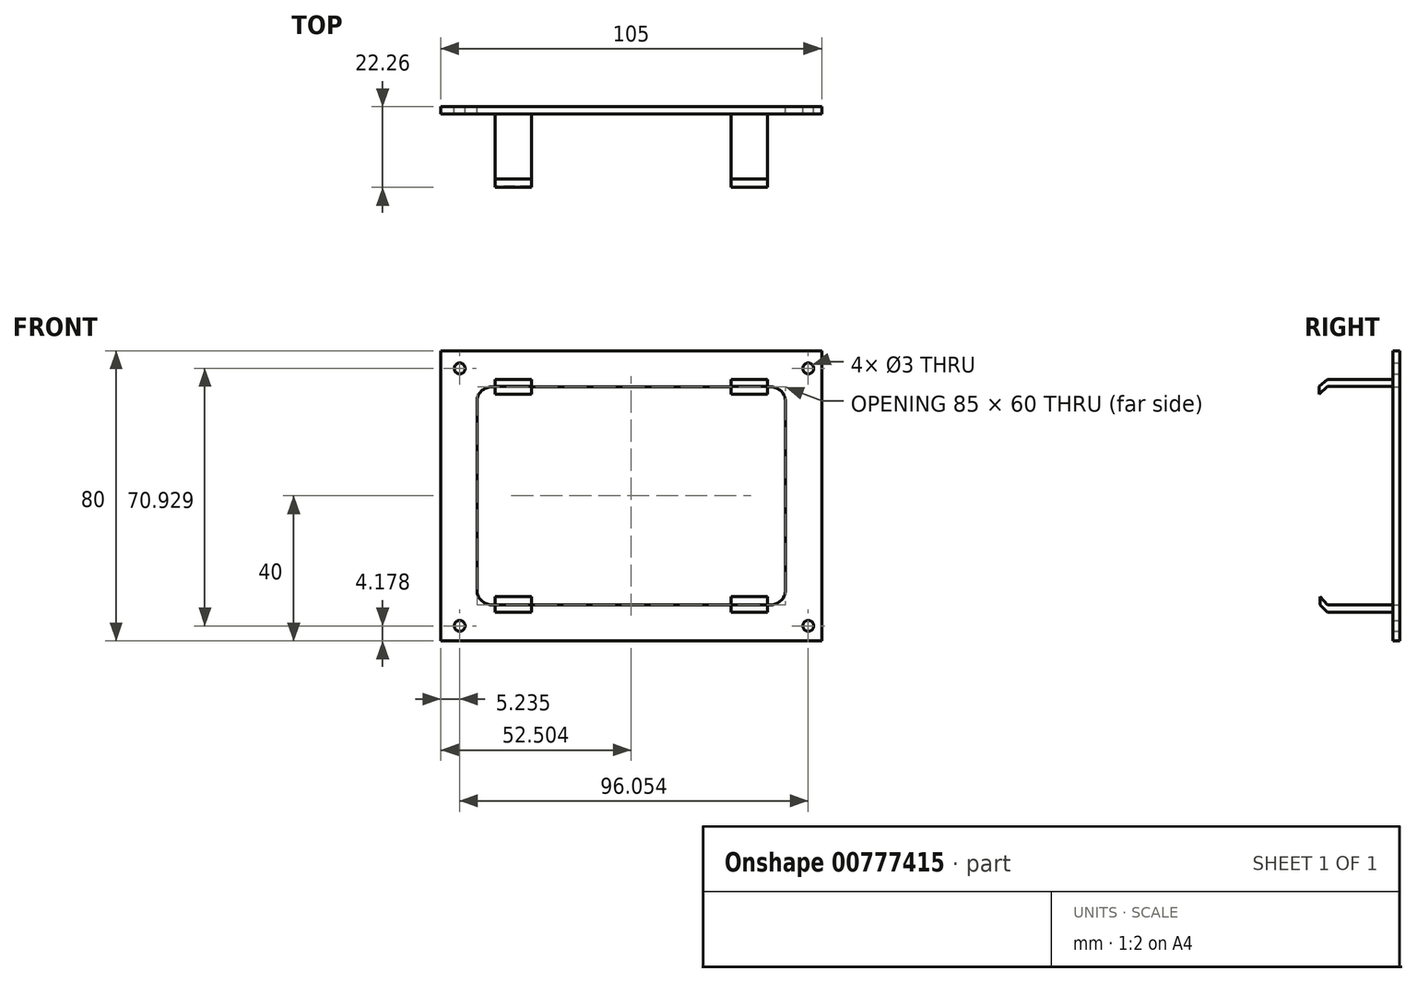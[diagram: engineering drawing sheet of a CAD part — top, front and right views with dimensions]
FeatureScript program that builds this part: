
annotation { "Feature Type Name" : "Feature", "Feature Type Description" : "" }
export const myFeature = defineFeature(function(context is Context, id is Id, definition is map)
    precondition{}
    {
        {
            var Q0;
            Q0=qCreatedBy(makeId("Front.planeOp"),FACE);
            var sketch = newSketch(context, id + "F0", { "sketchPlane" : qUnion([Q0])});
            skLineSegment(sketch, "E0.bottom", {"start": v(-34.06, 29.88) * mm, "end": v(42.94, 29.88) * mm});
            skLineSegment(sketch, "E0.top", {"start": v(-34.06, -30.12) * mm, "end": v(42.94, -30.12) * mm});
            skLineSegment(sketch, "E0.left", {"start": v(-38.06, 25.88) * mm, "end": v(-38.06, -26.12) * mm});
            skLineSegment(sketch, "E0.right", {"start": v(46.94, 25.88) * mm, "end": v(46.94, -26.12) * mm});
            skLineSegment(sketch, "E1.0", {"start": v(-48.06, 39.88) * mm, "end": v(56.94, 39.88) * mm});
            skLineSegment(sketch, "E1.1", {"start": v(-48.06, 39.88) * mm, "end": v(-48.06, -40.12) * mm});
            skLineSegment(sketch, "E1.2", {"start": v(-48.06, -40.12) * mm, "end": v(56.94, -40.12) * mm});
            skLineSegment(sketch, "E1.3", {"start": v(56.94, 39.88) * mm, "end": v(56.94, -40.12) * mm});
            skPoint(sketch, "E2", {"position": v(-42.82, 34.99) * mm});
            skPoint(sketch, "E3", {"position": v(-42.82, -35.94) * mm});
            skPoint(sketch, "E4", {"position": v(53.23, 34.99) * mm});
            skPoint(sketch, "E5", {"position": v(53.23, -35.94) * mm});
            skLineSegment(sketch, "E6.bottom", {"start": v(-33.06, 31.98) * mm, "end": v(-23.06, 31.98) * mm});
            skLineSegment(sketch, "E6.top", {"start": v(-33.06, 29.98) * mm, "end": v(-23.06, 29.98) * mm});
            skLineSegment(sketch, "E6.left", {"start": v(-33.06, 31.98) * mm, "end": v(-33.06, 29.98) * mm});
            skLineSegment(sketch, "E6.right", {"start": v(-23.06, 31.98) * mm, "end": v(-23.06, 29.98) * mm});
            skLineSegment(sketch, "E7.bottom", {"start": v(-33.06, -30.22) * mm, "end": v(-23.06, -30.22) * mm});
            skLineSegment(sketch, "E7.top", {"start": v(-33.06, -32.22) * mm, "end": v(-23.06, -32.22) * mm});
            skLineSegment(sketch, "E7.left", {"start": v(-33.06, -30.22) * mm, "end": v(-33.06, -32.22) * mm});
            skLineSegment(sketch, "E7.right", {"start": v(-23.06, -30.22) * mm, "end": v(-23.06, -32.22) * mm});
            skLineSegment(sketch, "E8.bottom", {"start": v(31.94, 31.98) * mm, "end": v(41.94, 31.98) * mm});
            skLineSegment(sketch, "E8.top", {"start": v(31.94, 29.98) * mm, "end": v(41.94, 29.98) * mm});
            skLineSegment(sketch, "E8.left", {"start": v(31.94, 31.98) * mm, "end": v(31.94, 29.98) * mm});
            skLineSegment(sketch, "E8.right", {"start": v(41.94, 31.98) * mm, "end": v(41.94, 29.98) * mm});
            skLineSegment(sketch, "E9.bottom", {"start": v(31.94, -30.22) * mm, "end": v(41.94, -30.22) * mm});
            skLineSegment(sketch, "E9.top", {"start": v(31.94, -32.22) * mm, "end": v(41.94, -32.22) * mm});
            skLineSegment(sketch, "E9.left", {"start": v(31.94, -30.22) * mm, "end": v(31.94, -32.22) * mm});
            skLineSegment(sketch, "E9.right", {"start": v(41.94, -30.22) * mm, "end": v(41.94, -32.22) * mm});
            skPoint(sketch, "E10.visualSharp", {"position": v(46.94, 29.88) * mm});
            skArc(sketch, "E10.filletArc", {"start": v(46.94, 25.88) * mm, "mid": v(45.77, 28.7) * mm, "end": v(42.94, 29.88) * mm});
            skPoint(sketch, "E11.visualSharp", {"position": v(46.94, -30.12) * mm});
            skArc(sketch, "E11.filletArc", {"start": v(42.94, -30.12) * mm, "mid": v(45.77, -28.95) * mm, "end": v(46.94, -26.12) * mm});
            skPoint(sketch, "E12.visualSharp", {"position": v(-38.06, 29.88) * mm});
            skArc(sketch, "E12.filletArc", {"start": v(-34.06, 29.88) * mm, "mid": v(-36.88, 28.7) * mm, "end": v(-38.06, 25.88) * mm});
            skPoint(sketch, "E13.visualSharp", {"position": v(-38.06, -30.12) * mm});
            skArc(sketch, "E13.filletArc", {"start": v(-38.06, -26.12) * mm, "mid": v(-36.88, -28.95) * mm, "end": v(-34.06, -30.12) * mm});
            skSolve(sketch);
        }
        {
            var Q0;
            Q0=makeQuery(id+"F0.imprint","IMPRINT",FACE,{"disambiguationData":[TD([[makeQuery(id+"F0.imprint","IMPRINT",EDGE,{"derivedFrom":sQuery(id+"F0.wireOp",EDGE,"E0.bottom")}),1.0]])]});
            extrude(context, id + "F1", {"entities" : qUnion([Q0]), "depth" : 2 * mm, "offsetDistance" : 25 * mm});
        }
        {
            var Q0;
            Q0=sQuery(id+"F0.wireOp",VERTEX,"E2");
            var Q1;
            Q1=sQuery(id+"F0.wireOp",VERTEX,"E3");
            var Q2;
            Q2=sQuery(id+"F0.wireOp",VERTEX,"E5");
            var Q3;
            Q3=sQuery(id+"F0.wireOp",VERTEX,"E4");
            var Q4;
            Q4=makeQuery(id+"F1.opExtrude","SWEPT_BODY",BODY,{"disambiguationData":[OSD([sQuery(id+"F0.wireOp",EDGE,"E0.bottom"),sQuery(id+"F0.wireOp",EDGE,"E0.top"),sQuery(id+"F0.wireOp",EDGE,"E0.left"),sQuery(id+"F0.wireOp",EDGE,"E0.right"),sQuery(id+"F0.wireOp",EDGE,"E1.0"),sQuery(id+"F0.wireOp",EDGE,"E1.1"),sQuery(id+"F0.wireOp",EDGE,"E1.2"),sQuery(id+"F0.wireOp",EDGE,"E1.3")])]});
            hole(context, id + "F2", {"style" : HoleStyle.SIMPLE, "endStyle" : HoleEndStyle.THROUGH, "oppositeDirection" : true, "holeDiameter" : 3 * mm, "majorDiameter" : 5 * mm, "isTappedThrough" : true, "tappedDepth" : 12 * mm, "tapClearance" : 3, "locations" : qUnion([Q0, Q1, Q2, Q3]), "scope" : qUnion([Q4])});
        }
        {
            var Q0;
            Q0=makeQuery(id+"F0.imprint","IMPRINT",FACE,{"disambiguationData":[TD([[makeQuery(id+"F0.imprint","IMPRINT",EDGE,{"derivedFrom":sQuery(id+"F0.wireOp",EDGE,"E6.bottom")}),-1.0]])]});
            var Q1;
            Q1=makeQuery(id+"F0.imprint","IMPRINT",FACE,{"disambiguationData":[TD([[makeQuery(id+"F0.imprint","IMPRINT",EDGE,{"derivedFrom":sQuery(id+"F0.wireOp",EDGE,"E8.bottom")}),-1.0]])]});
            var Q2;
            Q2=makeQuery(id+"F0.imprint","IMPRINT",FACE,{"disambiguationData":[TD([[makeQuery(id+"F0.imprint","IMPRINT",EDGE,{"derivedFrom":sQuery(id+"F0.wireOp",EDGE,"E7.bottom")}),-1.0]])]});
            var Q3;
            Q3=makeQuery(id+"F0.imprint","IMPRINT",FACE,{"disambiguationData":[TD([[makeQuery(id+"F0.imprint","IMPRINT",EDGE,{"derivedFrom":sQuery(id+"F0.wireOp",EDGE,"E9.bottom")}),-1.0]])]});
            extrude(context, id + "F3", {"entities" : qUnion([Q0, Q1, Q2, Q3]), "operationType" : NewBodyOperationType.ADD, "depth" : 20 * mm, "offsetDistance" : 25 * mm});
        }
        {
            var Q0;
            Q0=makeQuery(id+"F3.opExtrude","SWEPT_FACE",FACE,{"disambiguationData":[OSD([sQuery(id+"F0.wireOp",EDGE,"E6.left")])]});
            var sketch = newSketch(context, id + "F4", { "sketchPlane" : qUnion([Q0])});
            skLineSegment(sketch, "E14", {"start": v(20, 29.98) * mm, "end": v(22.26, 27.9) * mm});
            skLineSegment(sketch, "E15", {"start": v(22.26, 27.9) * mm, "end": v(22.26, 29.98) * mm});
            skLineSegment(sketch, "E16", {"start": v(22.26, 29.98) * mm, "end": v(20, 31.98) * mm});
            skLineSegment(sketch, "E17", {"start": v(20, 31.98) * mm, "end": v(20, 29.98) * mm});
            skSolve(sketch);
        }
        {
            var Q0;
            Q0=makeQuery(id+"F4.imprint","IMPRINT",FACE,{"disambiguationData":[TD([[makeQuery(id+"F4.imprint","IMPRINT",EDGE,{"derivedFrom":sQuery(id+"F4.wireOp",EDGE,"E14")}),1.0]])]});
            extrude(context, id + "F5", {"entities" : qUnion([Q0]), "operationType" : NewBodyOperationType.ADD, "oppositeDirection" : true, "depth" : 10 * mm, "offsetDistance" : 25 * mm});
        }
        {
            var Q0;
            Q0=makeQuery(id+"F3.opExtrude","SWEPT_FACE",FACE,{"disambiguationData":[OSD([sQuery(id+"F0.wireOp",EDGE,"E7.left")])]});
            var sketch = newSketch(context, id + "F6", { "sketchPlane" : qUnion([Q0])});
            skLineSegment(sketch, "E18", {"start": v(20, -30.22) * mm, "end": v(22.02, -27.92) * mm});
            skLineSegment(sketch, "E19", {"start": v(22.02, -27.92) * mm, "end": v(22.02, -30.22) * mm});
            skLineSegment(sketch, "E20", {"start": v(22.02, -30.22) * mm, "end": v(20, -32.22) * mm});
            skLineSegment(sketch, "E21", {"start": v(20, -32.22) * mm, "end": v(20, -30.22) * mm});
            skSolve(sketch);
        }
        {
            var Q0;
            Q0=makeQuery(id+"F6.imprint","IMPRINT",FACE,{"disambiguationData":[TD([[makeQuery(id+"F6.imprint","IMPRINT",EDGE,{"derivedFrom":sQuery(id+"F6.wireOp",EDGE,"E18")}),-1.0]])]});
            extrude(context, id + "F7", {"entities" : qUnion([Q0]), "operationType" : NewBodyOperationType.ADD, "oppositeDirection" : true, "depth" : 10 * mm, "offsetDistance" : 25 * mm});
        }
        {
            var Q0;
            Q0=makeQuery(id+"F3.opExtrude","SWEPT_FACE",FACE,{"disambiguationData":[OSD([sQuery(id+"F0.wireOp",EDGE,"E8.right")])]});
            var sketch = newSketch(context, id + "F8", { "sketchPlane" : qUnion([Q0])});
            skLineSegment(sketch, "E22", {"start": v(-20, 29.98) * mm, "end": v(-22.25, 27.89) * mm});
            skLineSegment(sketch, "E23", {"start": v(-22.25, 27.89) * mm, "end": v(-22.25, 29.98) * mm});
            skLineSegment(sketch, "E24", {"start": v(-22.25, 29.98) * mm, "end": v(-20, 31.98) * mm});
            skLineSegment(sketch, "E25", {"start": v(-20, 31.98) * mm, "end": v(-20, 29.98) * mm});
            skSolve(sketch);
        }
        {
            var Q0;
            Q0 = qSketchRegion(id + "F8", true);
            extrude(context, id + "F9", {"entities" : qUnion([Q0]), "operationType" : NewBodyOperationType.ADD, "oppositeDirection" : true, "depth" : 10 * mm, "offsetDistance" : 25 * mm});
        }
        {
            var Q0;
            Q0=makeQuery(id+"F3.opExtrude","SWEPT_FACE",FACE,{"disambiguationData":[OSD([sQuery(id+"F0.wireOp",EDGE,"E9.right")])]});
            var sketch = newSketch(context, id + "F10", { "sketchPlane" : qUnion([Q0])});
            skLineSegment(sketch, "E26", {"start": v(-20, -32.22) * mm, "end": v(-21.98, -30.22) * mm});
            skLineSegment(sketch, "E27", {"start": v(-21.98, -30.22) * mm, "end": v(-21.98, -27.9) * mm});
            skLineSegment(sketch, "E28", {"start": v(-21.98, -27.9) * mm, "end": v(-20, -30.22) * mm});
            skLineSegment(sketch, "E29", {"start": v(-20, -30.22) * mm, "end": v(-20, -32.22) * mm});
            skSolve(sketch);
        }
        {
            var Q0;
            Q0=makeQuery(id+"F10.imprint","IMPRINT",FACE,{"disambiguationData":[TD([[makeQuery(id+"F10.imprint","IMPRINT",EDGE,{"derivedFrom":sQuery(id+"F10.wireOp",EDGE,"E26")}),-1.0]])]});
            extrude(context, id + "F11", {"entities" : qUnion([Q0]), "operationType" : NewBodyOperationType.ADD, "oppositeDirection" : true, "depth" : 10 * mm, "offsetDistance" : 25 * mm});
        }
    });
